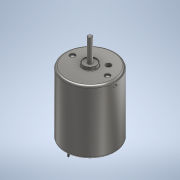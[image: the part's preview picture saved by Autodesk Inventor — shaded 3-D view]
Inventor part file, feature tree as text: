
AUTODESK INVENTOR PART (.ipt)
format: ipt  version: 2022 (Build 260153000, 153)  size: 342,016 bytes
history: native  units: mm
features: sketch x17, extrude x16, fillet x7, pattern_circular x5, other x2, hole x1, plane x1
ambient origin geometry x8: Origin, YZ Plane, XZ Plane, XY Plane, X Axis, Y Axis, Z Axis, Center Point
bodies: Solid1 (feature_tree)
feature tree (49):
  extrude  "Extrusion1"  Depth=30.8mm TaperAngle=0.0deg
  fillet  "Fillet1"  Radius=1.0mm
  extrude  "Extrusion4"  Depth=1.5mm
  fillet  "Fillet2"  Radius=1.5mm
  extrude  "Extrusion6"  Depth=0.25mm
  extrude  "Extrusion7"  Depth=1.2mm TaperAngle=0.0deg
  hole  "Hole1"  [1 undecoded]
  other  "Work Axis1"
  pattern_circular  "Circular Pattern1"  Count=2 Angle=360.0deg
  extrude  "Extrusion8"  Depth=2.0mm TaperAngle=0.0deg
  plane  "Work Plane1"
  extrude  "Extrusion9"  Depth=2.0mm
  pattern_circular  "Circular Pattern2"  Count=2 Angle=360.0deg
  extrude  "Extrusion10"  Depth=6.2mm
  extrude  "Extrusion11"  Depth=2.0mm
  extrude  "Extrusion12"  Depth=0.5mm
  extrude  "Extrusion13"  Depth=1.0mm
  extrude  "Extrusion14"  Depth=0.5mm TaperAngle=0.0deg
  extrude  "Extrusion15"  Depth=1.0mm TaperAngle=0.0deg
  extrude  "Extrusion16"  Depth=0.25mm
  pattern_circular  "Circular Pattern3"  [2 undecoded]
  fillet  "Fillet3"  [1 undecoded]
  extrude  "Extrusion17"  Depth=2.0mm TaperAngle=0.0deg
  pattern_circular  "Circular Pattern4"  [2 undecoded]
  extrude  "Extrusion18"  Depth=1.0mm
  extrude  "Extrusion19"  Depth=1.5mm
  fillet  "Fillet4"  Radius=1.5mm
  pattern_circular  "Circular Pattern5"  [2 undecoded]
  fillet  "Fillet5"  Radius=1.0mm
  fillet  "Fillet6"  Radius=0.25mm
  fillet  "Fillet7"  Radius=20.0mm
  sketch  "Sketch1"  dims[d0=24.4mm d1=30.8mm d2=0.0mm d9=1.0mm]
  sketch  "Sketch4"  dims[d10=6.4mm d11=6.0mm d12=1.5mm d13=0.0mm]
  sketch  "Sketch6"  dims[d14=0.25mm d18=5.8mm]
  sketch  "Sketch7"  dims[d19=2.2mm d20=1.2mm d21=0.0mm]
  sketch  "Sketch8"  dims[d22=2.0mm d23=12.5mm d24=0.0mm]
  sketch  "Sketch9"  dims[d26=8.5mm]
  sketch  "Sketch10"  dims[d27=2.459mm d28=0.8mm d29=4.0mm d30=2.0mm d31=90.0deg d32=0.8mm d33=20.594885mm d34=20.0mm d35=360.0deg]
  other  "Work Axis2"
  sketch  "Sketch11"  dims[d37=2.5mm d38=2.0mm d39=0.0mm]
  sketch  "Sketch12"  dims[d40=12.25mm d41=2.0mm]
  sketch  "Sketch13"  dims[d42=1.0mm d43=0.0mm d44=20.0mm d45=360.0deg]
  sketch  "Sketch14"  dims[d47=6.4mm d48=6.2mm]
  sketch  "Sketch15"  dims[d49=1.0mm d50=0.0mm d51=2.0mm]
  sketch  "Sketch16"  dims[d52=0.5mm d53=0.0mm d54=5.5mm]
  sketch  "Sketch17"  dims[d55=1.0mm d56=0.0mm d57=4.0mm]
  sketch  "Sketch18"  dims[d58=3.8mm d59=0.5mm d60=0.0mm]
  sketch  "Sketch19"  dims[d61=1.0mm d62=1.0mm d63=0.0mm]
  sketch  "Sketch20"  dims[d64=7.5mm d65=8.5mm d66=0.0mm d67=0.0mm d68=2.0mm d69=0.0mm d70=10.0mm d71=1.0mm d74=1.5mm d77=1.5mm d78=1.0mm d79=1.0mm d80=0.25mm d81=0.0mm d82=20.0mm d83=360.0deg d85=1.0mm d86=1.0mm d87=1.0mm d88=0.0mm d89=20.0mm d90=360.0deg d92=0.2mm d93=2.0mm d94=0.0mm d95=0.3mm d96=4.0mm d97=0.0mm d98=0.25mm d99=20.0mm d100=360.0deg d102=0.25mm d103=0.25mm d104=0.25mm]
note: 8 required parameter values undecoded (feature->parameter linkage not recoverable at this tier; creation-order binding heuristic only, values carry confidence <= 0.55)
